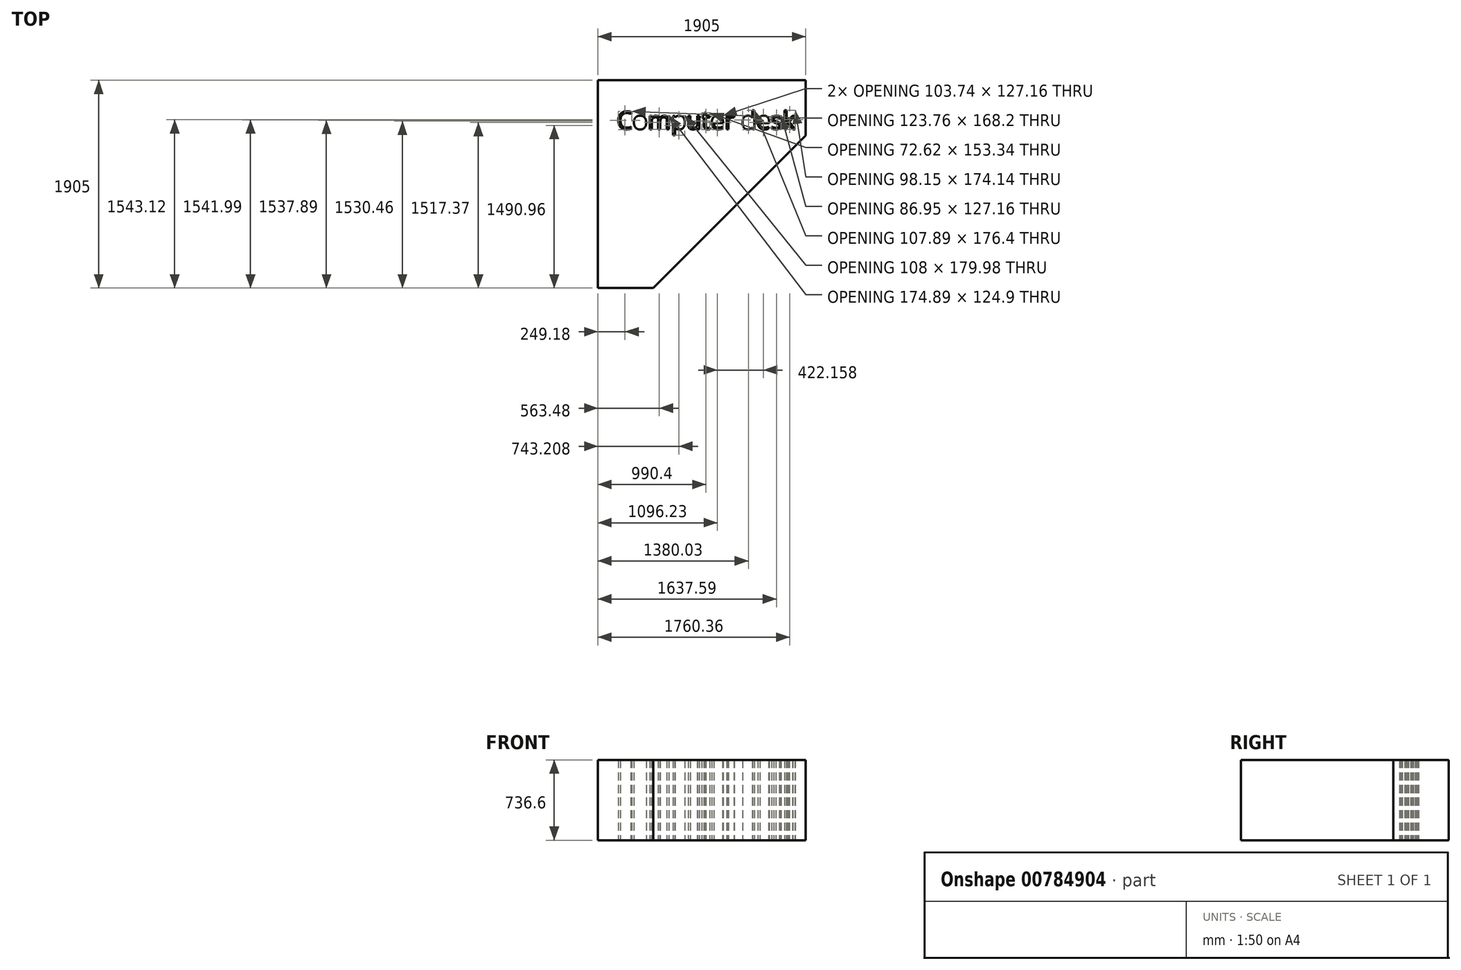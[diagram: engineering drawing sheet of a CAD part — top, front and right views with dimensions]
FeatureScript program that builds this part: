
annotation { "Feature Type Name" : "Feature", "Feature Type Description" : "" }
export const myFeature = defineFeature(function(context is Context, id is Id, definition is map)
    precondition{}
    {
        {
            var Q0;
            Q0=qCreatedBy(makeId("Top.planeOp"),FACE);
            var sketch = newSketch(context, id + "F0", { "sketchPlane" : qUnion([Q0])});
            skLineSegment(sketch, "E0", {"start": v(0, 0) * mm, "end": v(0, -1905) * mm});
            skLineSegment(sketch, "E1", {"start": v(0, 0) * mm, "end": v(1905, 0) * mm});
            skLineSegment(sketch, "E2", {"start": v(0, -1905) * mm, "end": v(508, -1905) * mm});
            skLineSegment(sketch, "E3", {"start": v(1905, 0) * mm, "end": v(1905, -508) * mm});
            skLineSegment(sketch, "E4", {"start": v(1905, -508) * mm, "end": v(508, -1905) * mm});
            skText(sketch, "E5", { "text": "Computer desk", "fontName": "OpenSans-Regular.ttf"});
            const initialGuessF0  = {"E5": [0.1733, -0.44895, 1, 0, 0.16501]};
            skSetInitialGuess(sketch, initialGuessF0);
            skSolve(sketch);
        }
        {
            var Q0;
            Q0=makeQuery(id+"F0.imprint","IMPRINT",FACE,{"disambiguationData":[TD([[makeQuery(id+"F0.imprint","IMPRINT",EDGE,{"derivedFrom":sQuery(id+"F0.wireOp",EDGE,"E0")}),1.0]])]});
            extrude(context, id + "F1", {"entities" : qUnion([Q0]), "depth" : 736.6 * mm, "offsetDistance" : 25.4 * mm});
        }
    });
